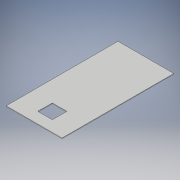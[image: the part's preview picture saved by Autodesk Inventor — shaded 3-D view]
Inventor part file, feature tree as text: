
AUTODESK INVENTOR PART (.ipt)
format: ipt  version: 2018 (Build 220112000, 112)  size: 122,880 bytes
history: native  units: mm
features: extrude x2, sketch x2, projected_geometry x1
ambient origin geometry x8: Origin, YZ Plane, XZ Plane, XY Plane, X Axis, Y Axis, Z Axis, Center Point
bodies: Volumenkörper1 (feature_tree)
feature tree (5):
  extrude  "Bodenplatte"  Depth=1.5mm
  extrude  "Extrusion5"  Depth=10.0mm
  sketch  "Skizze1"  dims[d2=1.5mm d3=1.5mm]
  sketch  "Skizze6"  dims[d4=1.5mm d5=150.0mm d6=305.0mm d7=1.8mm d8=0.0mm d18=40.0mm d19=40.0mm d20=30.0mm d21=1.2mm d22=1.2mm d23=1.2mm d24=1.2mm d25=10.0mm d26=0.0mm]
  projected_geometry  "Projizierte Kontur1"
